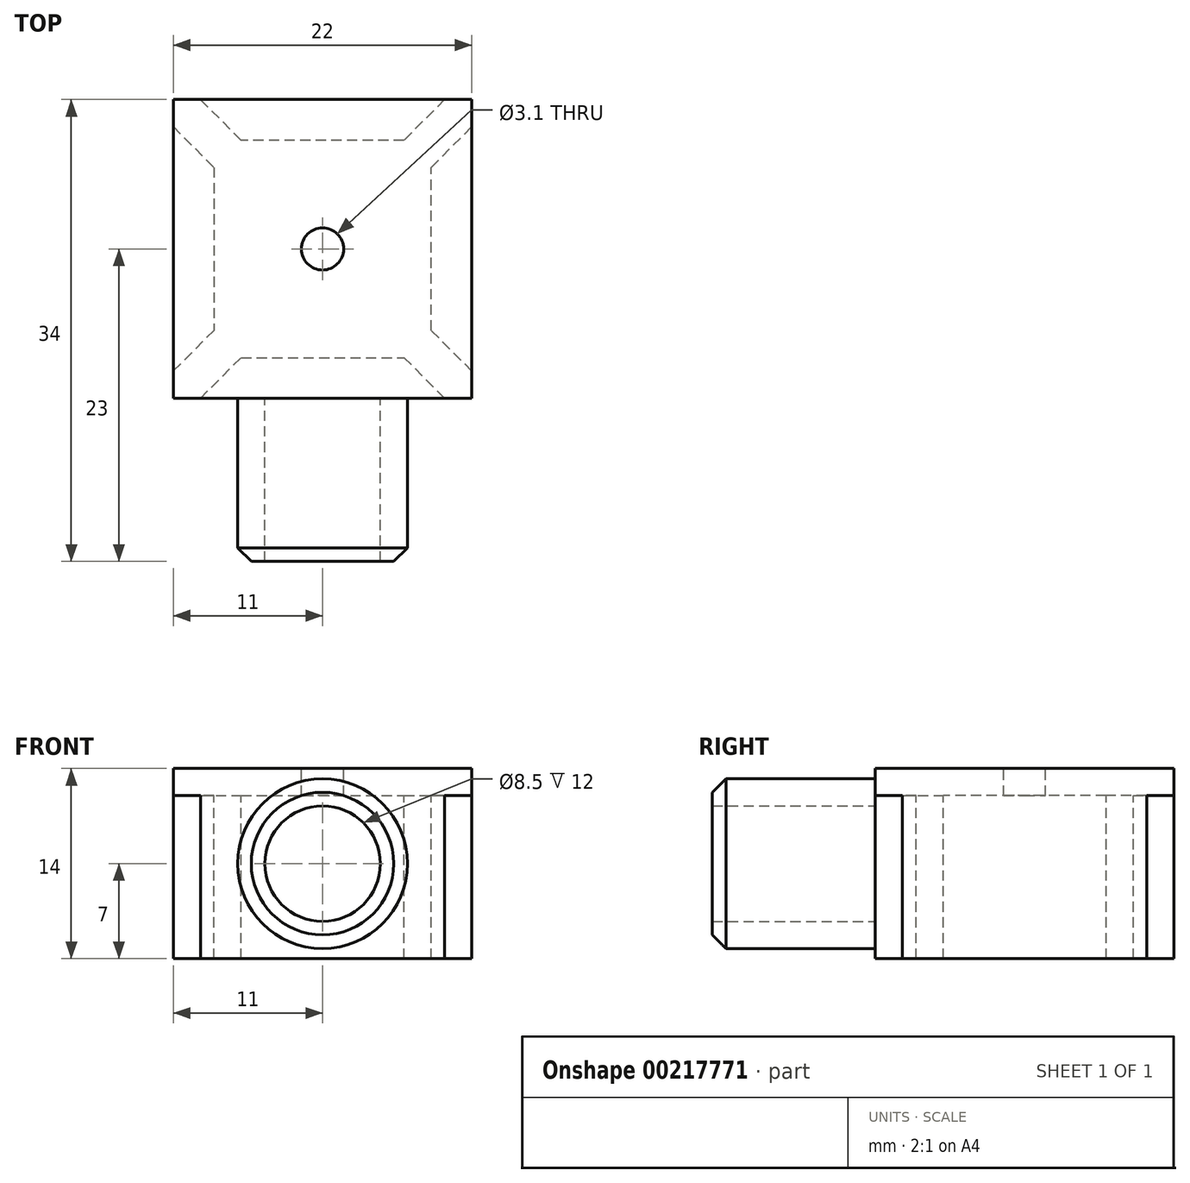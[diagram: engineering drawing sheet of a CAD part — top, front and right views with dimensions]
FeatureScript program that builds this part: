
annotation { "Feature Type Name" : "Feature", "Feature Type Description" : "" }
export const myFeature = defineFeature(function(context is Context, id is Id, definition is map)
    precondition{}
    {
        {
            var Q0;
            Q0=qCreatedBy(makeId("Top.planeOp"),FACE);
            var sketch = newSketch(context, id + "F0", { "sketchPlane" : qUnion([Q0])});
            skLineSegment(sketch, "E0.bottom", {"start": v(-11, 11) * mm, "end": v(11, 11) * mm});
            skLineSegment(sketch, "E0.top", {"start": v(-11, -11) * mm, "end": v(11, -11) * mm});
            skLineSegment(sketch, "E0.left", {"start": v(-11, 11) * mm, "end": v(-11, -11) * mm});
            skLineSegment(sketch, "E0.right", {"start": v(11, 11) * mm, "end": v(11, -11) * mm});
            skPoint(sketch, "E0.middle", {"position": v(0, 0) * mm});
            skSolve(sketch);
        }
        {
            var Q0;
            Q0 = qSketchRegion(id + "F0", true);
            extrude(context, id + "F1", {"entities" : qUnion([Q0]), "depth" : 2 * mm});
        }
        {
            var Q0;
            Q0=makeQuery(id+"F1.opExtrude","CAP_FACE",FACE,{"disambiguationData":[OSD([sQuery(id+"F0.wireOp",EDGE,"E0.bottom"),sQuery(id+"F0.wireOp",EDGE,"E0.top"),sQuery(id+"F0.wireOp",EDGE,"E0.left"),sQuery(id+"F0.wireOp",EDGE,"E0.right")])],"isStart":false});
            var sketch = newSketch(context, id + "F2", { "sketchPlane" : qUnion([Q0])});
            skCircle(sketch, "E1", {"center": v(0, 0) * mm, "radius": 1.55 * mm});
            skSolve(sketch);
        }
        {
            var Q0;
            Q0 = qSketchRegion(id + "F2", true);
            extrude(context, id + "F3", {"entities" : qUnion([Q0]), "operationType" : NewBodyOperationType.REMOVE, "endBound" : BoundingType.THROUGH_ALL, "oppositeDirection" : true, "depth" : 25 * mm});
        }
        {
            var Q0;
            Q0=makeQuery(id+"F1.opExtrude","CAP_FACE",FACE,{"disambiguationData":[OSD([sQuery(id+"F0.wireOp",EDGE,"E0.bottom"),sQuery(id+"F0.wireOp",EDGE,"E0.top"),sQuery(id+"F0.wireOp",EDGE,"E0.left"),sQuery(id+"F0.wireOp",EDGE,"E0.right")])],"isStart":true});
            var sketch = newSketch(context, id + "F4", { "sketchPlane" : qUnion([Q0])});
            skLineSegment(sketch, "E2", {"start": v(-9, 11) * mm, "end": v(-6, 8) * mm});
            skLineSegment(sketch, "E3", {"start": v(-6, 8) * mm, "end": v(6, 8) * mm});
            skLineSegment(sketch, "E4", {"start": v(6, 8) * mm, "end": v(9, 11) * mm});
            skLineSegment(sketch, "E5", {"start": v(9, 11) * mm, "end": v(-9, 11) * mm});
            skLineSegment(sketch, "E6.1.0", {"start": v(-11, 9) * mm, "end": v(-11, -9) * mm});
            skLineSegment(sketch, "E6.1.1", {"start": v(-8, 6) * mm, "end": v(-11, 9) * mm});
            skLineSegment(sketch, "E6.1.2", {"start": v(-8, -6) * mm, "end": v(-8, 6) * mm});
            skLineSegment(sketch, "E6.1.3", {"start": v(-11, -9) * mm, "end": v(-8, -6) * mm});
            skLineSegment(sketch, "E6.2.0", {"start": v(-9, -11) * mm, "end": v(9, -11) * mm});
            skLineSegment(sketch, "E6.2.1", {"start": v(-6, -8) * mm, "end": v(-9, -11) * mm});
            skLineSegment(sketch, "E6.2.2", {"start": v(6, -8) * mm, "end": v(-6, -8) * mm});
            skLineSegment(sketch, "E6.2.3", {"start": v(9, -11) * mm, "end": v(6, -8) * mm});
            skLineSegment(sketch, "E6.3.0", {"start": v(11, -9) * mm, "end": v(11, 9) * mm});
            skLineSegment(sketch, "E6.3.1", {"start": v(8, -6) * mm, "end": v(11, -9) * mm});
            skLineSegment(sketch, "E6.3.2", {"start": v(8, 6) * mm, "end": v(8, -6) * mm});
            skLineSegment(sketch, "E6.3.3", {"start": v(11, 9) * mm, "end": v(8, 6) * mm});
            skPoint(sketch, "E6.center", {"position": v(0, 0) * mm});
            skSolve(sketch);
        }
        {
            var Q0;
            Q0 = qSketchRegion(id + "F4", true);
            extrude(context, id + "F5", {"entities" : qUnion([Q0]), "operationType" : NewBodyOperationType.ADD, "depth" : 12 * mm});
        }
        {
            var Q0;
            Q0=makeQuery(id+"F5.boolean.opBoolean","MERGE",FACE,{"derivedFrom":[makeQuery(id+"F1.opExtrude","SWEPT_FACE",FACE,{"disambiguationData":[OSD([sQuery(id+"F0.wireOp",EDGE,"E0.top")])]}),makeQuery(id+"F5.opExtrude","SWEPT_FACE",FACE,{"disambiguationData":[OSD([sQuery(id+"F4.wireOp",EDGE,"E5")])]})]});
            var sketch = newSketch(context, id + "F6", { "sketchPlane" : qUnion([Q0])});
            skLineSegment(sketch, "E7", {"start": v(0, 2) * mm, "end": v(0, -12) * mm, "construction": true});
            skCircle(sketch, "E8", {"center": v(0, -5) * mm, "radius": 6.25 * mm});
            skCircle(sketch, "E9", {"center": v(0, -5) * mm, "radius": 4.25 * mm});
            skSolve(sketch);
        }
        {
            var Q0;
            Q0 = qSketchRegion(id + "F6", true);
            extrude(context, id + "F7", {"entities" : qUnion([Q0]), "operationType" : NewBodyOperationType.ADD, "depth" : 12 * mm});
        }
        {
            var Q0;
            Q0=makeQuery(id+"F7.opExtrude","CAP_EDGE",EDGE,{"disambiguationData":[OSD([sQuery(id+"F6.wireOp",EDGE,"E8")])],"isStart":false});
            chamfer(context, id + "F8", {"entities" : qUnion([Q0]), "width" : 1 * mm, "tangentPropagation" : true});
        }
    });
